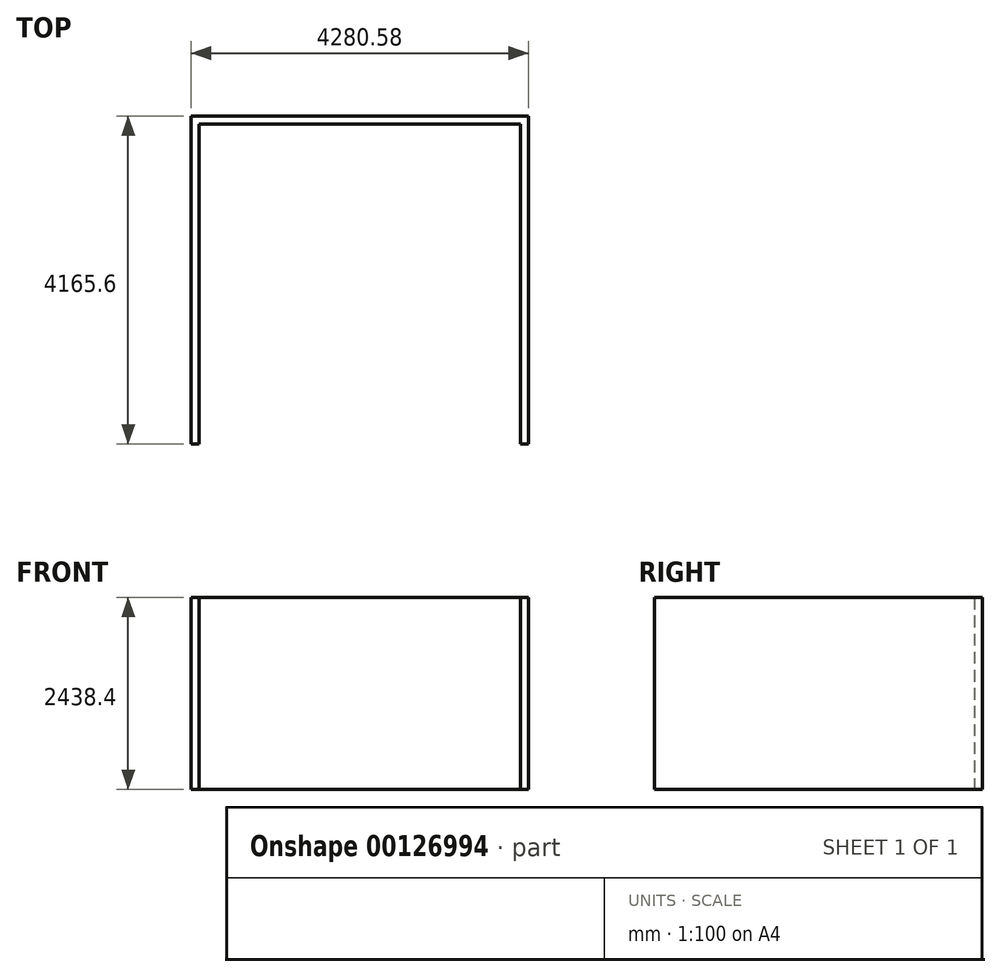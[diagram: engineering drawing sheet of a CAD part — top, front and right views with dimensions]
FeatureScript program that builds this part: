
annotation { "Feature Type Name" : "Feature", "Feature Type Description" : "" }
export const myFeature = defineFeature(function(context is Context, id is Id, definition is map)
    precondition{}
    {
        {
            var Q0;
            Q0=qCreatedBy(makeId("Top.planeOp"),FACE);
            var sketch = newSketch(context, id + "F0", { "sketchPlane" : qUnion([Q0])});
            skLineSegment(sketch, "E0", {"start": v(0, 0) * mm, "end": v(0, 4064) * mm});
            skLineSegment(sketch, "E1", {"start": v(0, 4064) * mm, "end": v(4077.38, 4064) * mm});
            skLineSegment(sketch, "E2", {"start": v(4077.38, 4064) * mm, "end": v(4077.38, 0) * mm});
            skLineSegment(sketch, "E3.0", {"start": v(4178.98, 4165.6) * mm, "end": v(4178.98, 0) * mm});
            skLineSegment(sketch, "E3.1", {"start": v(-101.6, 4165.6) * mm, "end": v(4178.98, 4165.6) * mm});
            skLineSegment(sketch, "E3.2", {"start": v(-101.6, 0) * mm, "end": v(-101.6, 4165.6) * mm});
            skLineSegment(sketch, "E4", {"start": v(4077.38, 0) * mm, "end": v(4178.98, 0) * mm});
            skLineSegment(sketch, "E5", {"start": v(0, 0) * mm, "end": v(-101.6, 0) * mm});
            skSolve(sketch);
        }
        {
            var Q0;
            Q0 = qSketchRegion(id + "F0", true);
            extrude(context, id + "F1", {"entities" : qUnion([Q0]), "depth" : 2438.4 * mm});
        }
    });
